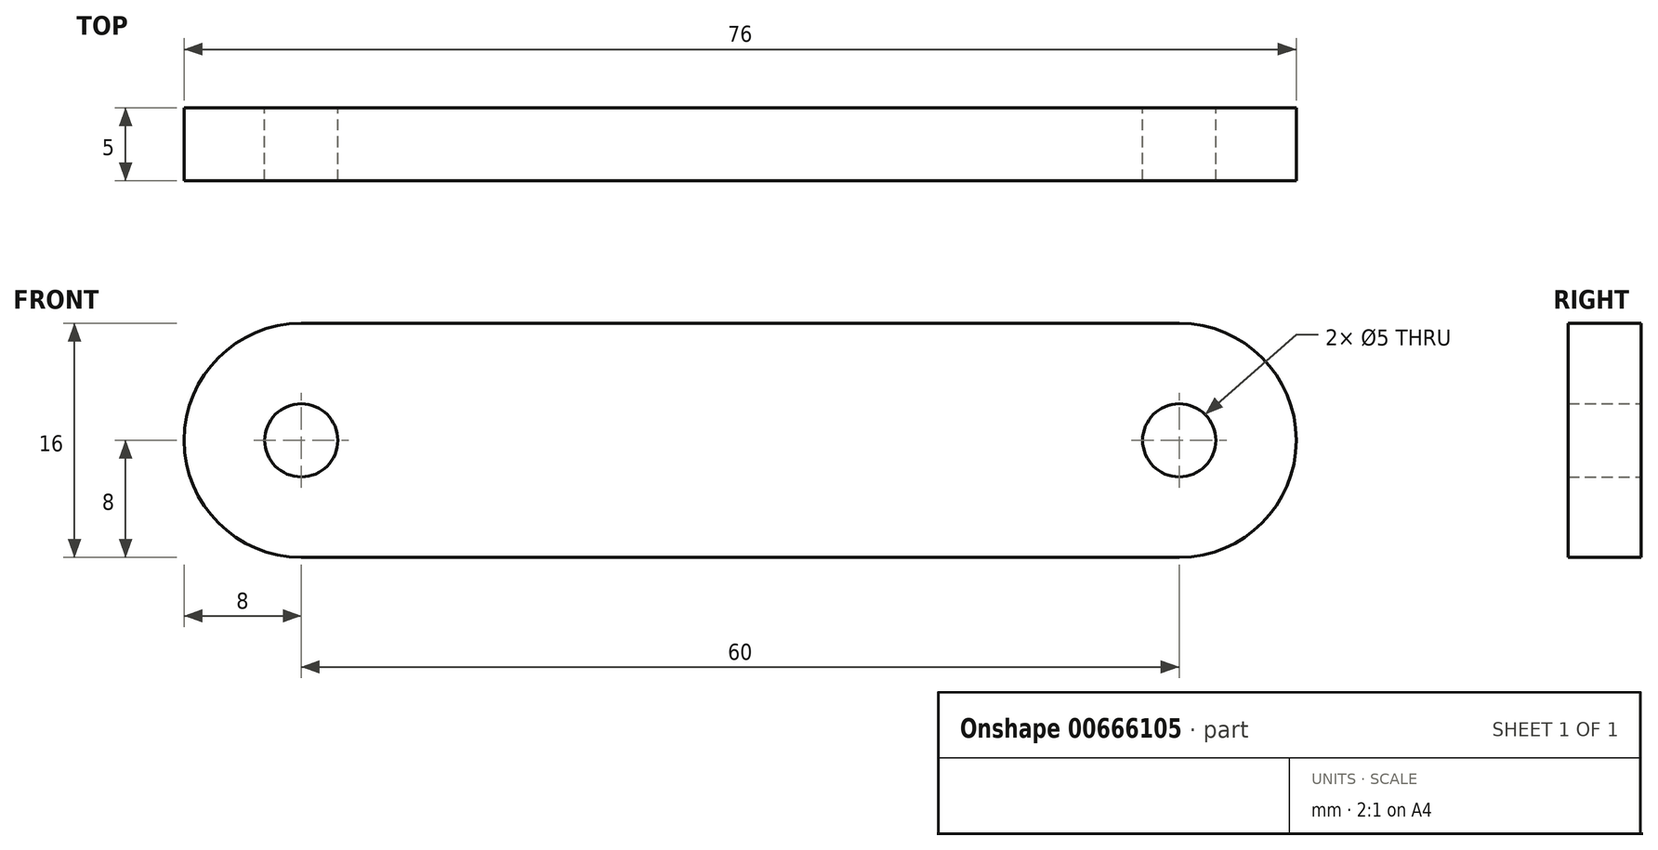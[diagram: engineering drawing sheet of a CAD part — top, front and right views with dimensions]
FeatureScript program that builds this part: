
annotation { "Feature Type Name" : "Feature", "Feature Type Description" : "" }
export const myFeature = defineFeature(function(context is Context, id is Id, definition is map)
    precondition{}
    {
        {
            var Q0;
            Q0=qCreatedBy(makeId("Front.planeOp"),FACE);
            var sketch = newSketch(context, id + "F0", { "sketchPlane" : qUnion([Q0])});
            skLineSegment(sketch, "E0.bottom", {"start": v(-30, 8) * mm, "end": v(30, 8) * mm});
            skLineSegment(sketch, "E0.top", {"start": v(-30, -8) * mm, "end": v(30, -8) * mm});
            skArc(sketch, "E1", {"start": v(-30, 8) * mm, "mid": v(-38, 0) * mm, "end": v(-30, -8) * mm});
            skArc(sketch, "E2", {"start": v(30, -8) * mm, "mid": v(38, 0) * mm, "end": v(30, 8) * mm});
            skCircle(sketch, "E3", {"center": v(-30, 0) * mm, "radius": 2.5 * mm});
            skCircle(sketch, "E4", {"center": v(30, 0) * mm, "radius": 2.5 * mm});
            skSolve(sketch);
        }
        {
            var Q0;
            Q0=makeQuery(id+"F0.imprint","IMPRINT",FACE,{"disambiguationData":[TD([[makeQuery(id+"F0.imprint","IMPRINT",EDGE,{"derivedFrom":sQuery(id+"F0.wireOp",EDGE,"E0.bottom")}),-1.0]])]});
            extrude(context, id + "F1", {"entities" : qUnion([Q0]), "depth" : 5 * mm, "offsetDistance" : 25 * mm});
        }
    });
